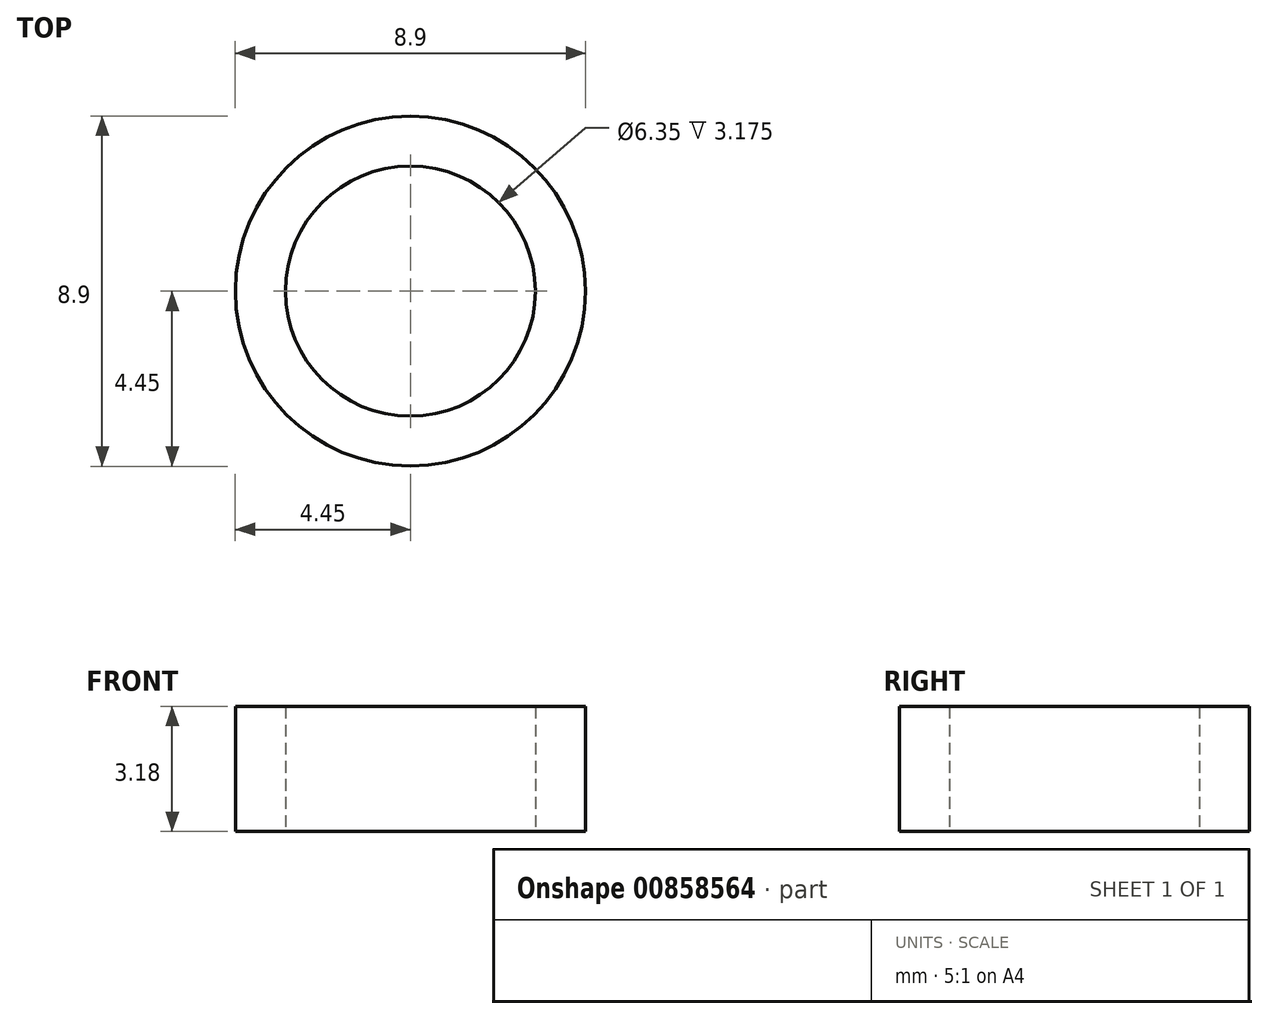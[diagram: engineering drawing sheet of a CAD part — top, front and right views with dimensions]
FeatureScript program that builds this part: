
annotation { "Feature Type Name" : "Feature", "Feature Type Description" : "" }
export const myFeature = defineFeature(function(context is Context, id is Id, definition is map)
    precondition{}
    {
        {
            var Q0;
            Q0=qCreatedBy(makeId("Top.planeOp"),FACE);
            var sketch = newSketch(context, id + "F0", { "sketchPlane" : qUnion([Q0])});
            skCircle(sketch, "E0", {"center": v(0, 0) * mm, "radius": 3.18 * mm});
            skCircle(sketch, "E1.0", {"center": v(0, 0) * mm, "radius": 4.45 * mm});
            skSolve(sketch);
        }
        {
            var Q0;
            Q0=makeQuery(id+"F0.imprint","IMPRINT",FACE,{"disambiguationData":[TD([[makeQuery(id+"F0.imprint","IMPRINT",EDGE,{"derivedFrom":sQuery(id+"F0.wireOp",EDGE,"E0")}),-1.0]])]});
            extrude(context, id + "F1", {"entities" : qUnion([Q0]), "depth" : 3.17 * mm, "offsetDistance" : 25.4 * mm});
        }
    });
